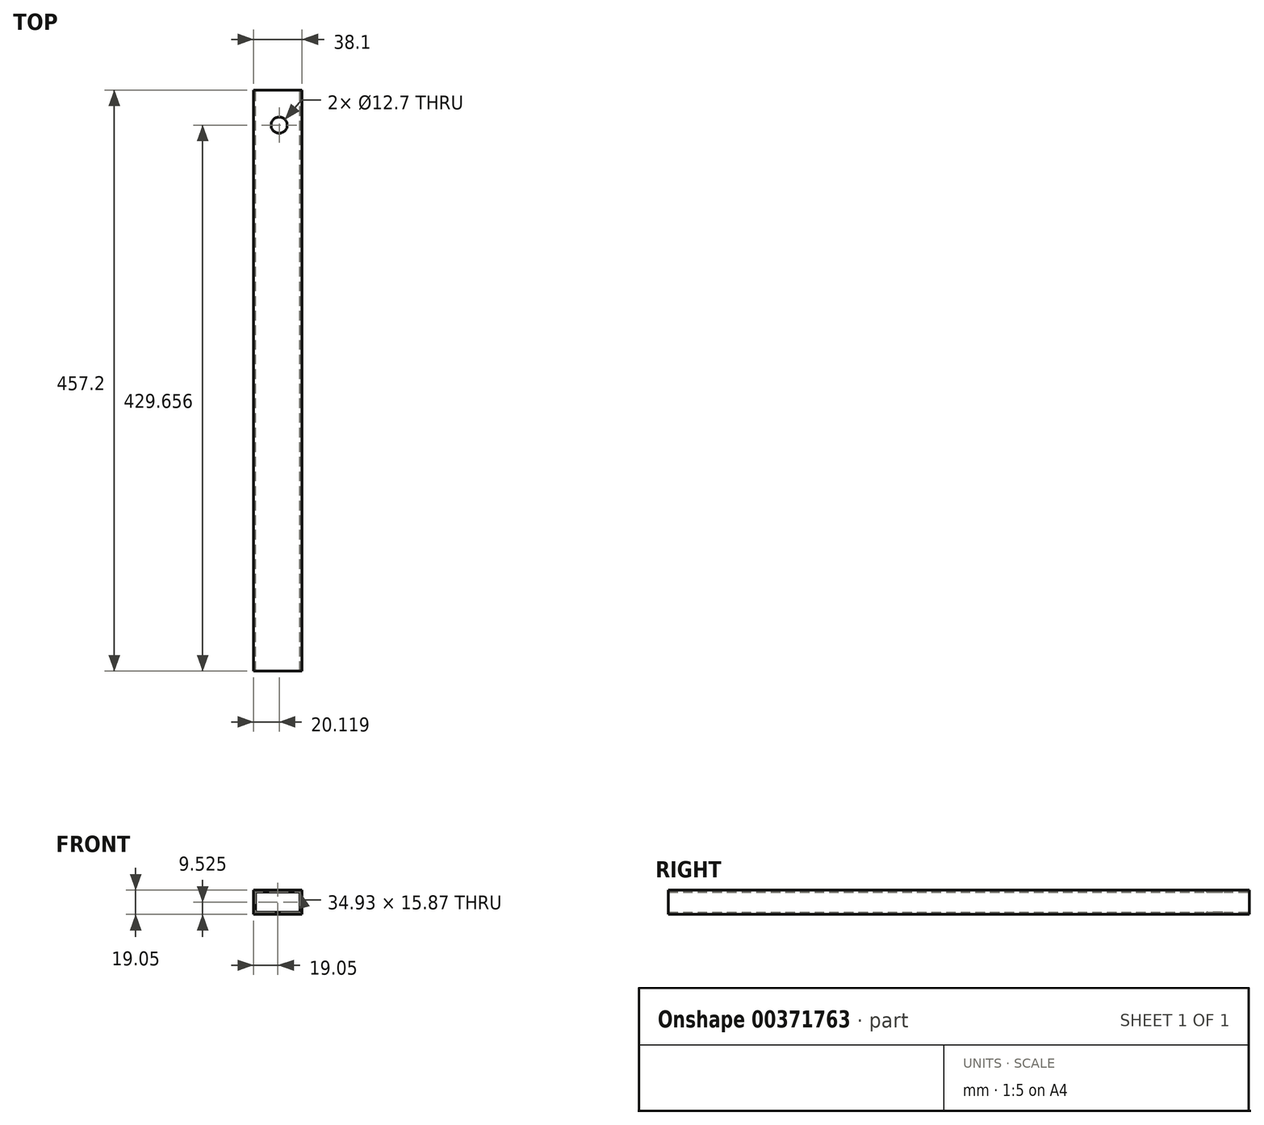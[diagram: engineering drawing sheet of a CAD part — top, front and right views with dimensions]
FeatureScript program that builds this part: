
annotation { "Feature Type Name" : "Feature", "Feature Type Description" : "" }
export const myFeature = defineFeature(function(context is Context, id is Id, definition is map)
    precondition{}
    {
        {
            var Q0;
            Q0=qCreatedBy(makeId("Front.planeOp"),FACE);
            var sketch = newSketch(context, id + "F0", { "sketchPlane" : qUnion([Q0])});
            skLineSegment(sketch, "E0.bottom", {"start": v(0, 0) * mm, "end": v(38.1, 0) * mm});
            skLineSegment(sketch, "E0.top", {"start": v(0, 19.05) * mm, "end": v(38.1, 19.05) * mm});
            skLineSegment(sketch, "E0.left", {"start": v(0, 0) * mm, "end": v(0, 19.05) * mm});
            skLineSegment(sketch, "E0.right", {"start": v(38.1, 0) * mm, "end": v(38.1, 19.05) * mm});
            skLineSegment(sketch, "E1.bottom", {"start": v(1.59, 1.59) * mm, "end": v(36.51, 1.59) * mm});
            skLineSegment(sketch, "E1.top", {"start": v(1.59, 17.46) * mm, "end": v(36.51, 17.46) * mm});
            skLineSegment(sketch, "E1.left", {"start": v(1.59, 1.59) * mm, "end": v(1.59, 17.46) * mm});
            skLineSegment(sketch, "E1.right", {"start": v(36.51, 1.59) * mm, "end": v(36.51, 17.46) * mm});
            skSolve(sketch);
        }
        {
            var Q0;
            Q0=makeQuery(id+"F0.imprint","IMPRINT",FACE,{"disambiguationData":[TD([[makeQuery(id+"F0.imprint","IMPRINT",EDGE,{"derivedFrom":sQuery(id+"F0.wireOp",EDGE,"E0.bottom")}),1.0]])]});
            extrude(context, id + "F1", {"entities" : qUnion([Q0]), "depth" : 457.2 * mm});
        }
        {
            var Q0;
            Q0=makeQuery(id+"F1.opExtrude","SWEPT_FACE",FACE,{"disambiguationData":[OSD([sQuery(id+"F0.wireOp",EDGE,"E0.top")])]});
            var sketch = newSketch(context, id + "F2", { "sketchPlane" : qUnion([Q0])});
            skCircle(sketch, "E2", {"center": v(20.12, -27.54) * mm, "radius": 6.38 * mm});
            skSolve(sketch);
        }
        {
            var Q0;
            Q0=sQuery(id+"F2.wireOp",VERTEX,"E2.center");
            var Q1;
            Q1=makeQuery(id+"F1.opExtrude","SWEPT_BODY",BODY,{"disambiguationData":[OSD([sQuery(id+"F0.wireOp",EDGE,"E0.bottom"),sQuery(id+"F0.wireOp",EDGE,"E0.top"),sQuery(id+"F0.wireOp",EDGE,"E0.left"),sQuery(id+"F0.wireOp",EDGE,"E0.right"),sQuery(id+"F0.wireOp",EDGE,"E1.bottom"),sQuery(id+"F0.wireOp",EDGE,"E1.top"),sQuery(id+"F0.wireOp",EDGE,"E1.left"),sQuery(id+"F0.wireOp",EDGE,"E1.right")])]});
            hole(context, id + "F3", {"style" : HoleStyle.SIMPLE, "endStyle" : HoleEndStyle.THROUGH, "holeDiameter" : 12.7 * mm, "isTappedThrough" : true, "tappedDepth" : 12.7 * mm, "tapClearance" : 3, "locations" : qUnion([Q0]), "scope" : qUnion([Q1])});
        }
    });
